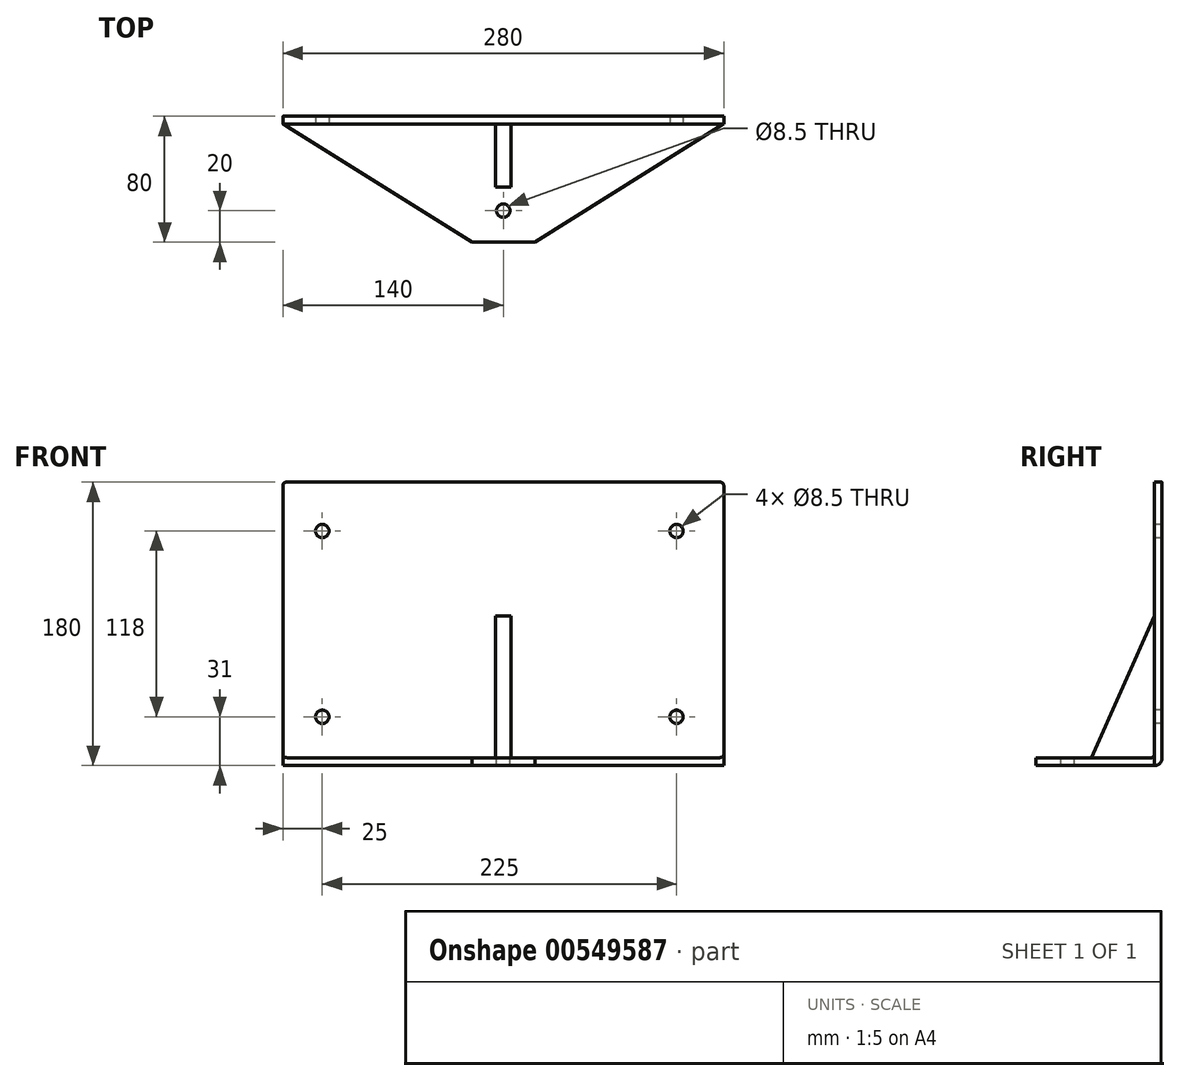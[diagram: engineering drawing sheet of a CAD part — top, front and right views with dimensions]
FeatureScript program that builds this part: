
annotation { "Feature Type Name" : "Feature", "Feature Type Description" : "" }
export const myFeature = defineFeature(function(context is Context, id is Id, definition is map)
    precondition{}
    {
        {
            var Q0;
            Q0=qCreatedBy(makeId("Right.planeOp"),FACE);
            var sketch = newSketch(context, id + "F0", { "sketchPlane" : qUnion([Q0])});
            skLineSegment(sketch, "E0", {"start": v(0, 90) * mm, "end": v(0, -90) * mm});
            skLineSegment(sketch, "E1", {"start": v(0, -90) * mm, "end": v(-80, -90) * mm});
            skLineSegment(sketch, "E2", {"start": v(-80, -90) * mm, "end": v(-80, -85) * mm});
            skLineSegment(sketch, "E3", {"start": v(-80, -85) * mm, "end": v(-5, -85) * mm});
            skLineSegment(sketch, "E4", {"start": v(-5, -85) * mm, "end": v(-5, 90) * mm});
            skLineSegment(sketch, "E5", {"start": v(-5, 90) * mm, "end": v(0, 90) * mm});
            skSolve(sketch);
        }
        {
            var Q0;
            Q0=makeQuery(id+"F0.imprint","IMPRINT",FACE,{"disambiguationData":[TD([[makeQuery(id+"F0.imprint","IMPRINT",EDGE,{"derivedFrom":sQuery(id+"F0.wireOp",EDGE,"E0")}),-1.0]])]});
            extrude(context, id + "F1", {"entities" : qUnion([Q0]), "depth" : 280 * mm, "offsetDistance" : 25 * mm});
        }
        {
            var Q0;
            Q0=makeQuery(id+"F1.opExtrude","SWEPT_FACE",FACE,{"disambiguationData":[OSD([sQuery(id+"F0.wireOp",EDGE,"E4")])]});
            var sketch = newSketch(context, id + "F2", { "sketchPlane" : qUnion([Q0])});
            skLineSegment(sketch, "E6", {"start": v(-180.39, 59) * mm, "end": v(443.82, 59) * mm, "construction": true});
            skLineSegment(sketch, "E7", {"start": v(-176.6, -59) * mm, "end": v(457.98, -59) * mm, "construction": true});
            skLineSegment(sketch, "E8", {"start": v(25, 195.64) * mm, "end": v(25, -196.32) * mm, "construction": true});
            skLineSegment(sketch, "E9", {"start": v(250, 193) * mm, "end": v(250, -198.95) * mm, "construction": true});
            skCircle(sketch, "E10", {"center": v(25, 59) * mm, "radius": 4.25 * mm});
            skCircle(sketch, "E11", {"center": v(250, 59) * mm, "radius": 4.25 * mm});
            skCircle(sketch, "E12", {"center": v(250, -59) * mm, "radius": 4.25 * mm});
            skCircle(sketch, "E13", {"center": v(25, -59) * mm, "radius": 4.25 * mm});
            skSolve(sketch);
        }
        {
            var Q0;
            Q0=makeQuery(id+"F2.imprint","IMPRINT",FACE,{"disambiguationData":[TD([[makeQuery(id+"F2.imprint","IMPRINT",EDGE,{"derivedFrom":sQuery(id+"F2.wireOp",EDGE,"E10")}),1.0]])]});
            var Q1;
            Q1=makeQuery(id+"F2.imprint","IMPRINT",FACE,{"disambiguationData":[TD([[makeQuery(id+"F2.imprint","IMPRINT",EDGE,{"derivedFrom":sQuery(id+"F2.wireOp",EDGE,"E13")}),1.0]])]});
            var Q2;
            Q2=makeQuery(id+"F2.imprint","IMPRINT",FACE,{"disambiguationData":[TD([[makeQuery(id+"F2.imprint","IMPRINT",EDGE,{"derivedFrom":sQuery(id+"F2.wireOp",EDGE,"E12")}),1.0]])]});
            var Q3;
            Q3=makeQuery(id+"F2.imprint","IMPRINT",FACE,{"disambiguationData":[TD([[makeQuery(id+"F2.imprint","IMPRINT",EDGE,{"derivedFrom":sQuery(id+"F2.wireOp",EDGE,"E11")}),1.0]])]});
            extrude(context, id + "F3", {"entities" : qUnion([Q0, Q1, Q2, Q3]), "operationType" : NewBodyOperationType.REMOVE, "endBound" : BoundingType.THROUGH_ALL, "oppositeDirection" : true, "depth" : 25 * mm, "offsetDistance" : 25 * mm});
        }
        {
            var Q0;
            Q0=makeQuery(id+"F1.opExtrude","CAP_EDGE",EDGE,{"disambiguationData":[OSD([sQuery(id+"F0.wireOp",EDGE,"E5")])],"isStart":true});
            var Q1;
            Q1=makeQuery(id+"F1.opExtrude","CAP_EDGE",EDGE,{"disambiguationData":[OSD([sQuery(id+"F0.wireOp",EDGE,"E5")])],"isStart":false});
            var Q2;
            Q2=makeQuery(id+"F1.opExtrude","CAP_EDGE",EDGE,{"disambiguationData":[OSD([sQuery(id+"F0.wireOp",EDGE,"E2")])],"isStart":false});
            var Q3;
            Q3=makeQuery(id+"F1.opExtrude","CAP_EDGE",EDGE,{"disambiguationData":[OSD([sQuery(id+"F0.wireOp",EDGE,"E2")])],"isStart":true});
            fillet(context, id + "F4", {"entities" : qUnion([Q0, Q1, Q2, Q3]), "radius" : 2 * mm, "tangentPropagation" : true, "allowEdgeOverflow" : false});
        }
        {
            var Q0;
            Q0=makeQuery(id+"F1.opExtrude","SWEPT_FACE",FACE,{"disambiguationData":[OSD([sQuery(id+"F0.wireOp",EDGE,"E3")])]});
            var sketch = newSketch(context, id + "F5", { "sketchPlane" : qUnion([Q0])});
            skLineSegment(sketch, "E14", {"start": v(40.82, -60) * mm, "end": v(230.6, -60) * mm, "construction": true});
            skLineSegment(sketch, "E15", {"start": v(140, -5) * mm, "end": v(140, -80) * mm, "construction": true});
            skCircle(sketch, "E16", {"center": v(140, -60) * mm, "radius": 4.25 * mm});
            skSolve(sketch);
        }
        {
            var Q0;
            Q0=makeQuery(id+"F5.imprint","IMPRINT",FACE,{"disambiguationData":[TD([[makeQuery(id+"F5.imprint","IMPRINT",EDGE,{"derivedFrom":sQuery(id+"F5.wireOp",EDGE,"E16")}),1.0]])]});
            extrude(context, id + "F6", {"entities" : qUnion([Q0]), "operationType" : NewBodyOperationType.REMOVE, "endBound" : BoundingType.THROUGH_ALL, "oppositeDirection" : true, "depth" : 25 * mm, "offsetDistance" : 25 * mm});
        }
        {
            var Q0;
            Q0=makeQuery(id+"F1.opExtrude","SWEPT_EDGE",EDGE,{"disambiguationData":[OSD([sQuery(id+"F0.wireOp",EDGE,"E0"),sQuery(id+"F0.wireOp",EDGE,"E1")])]});
            fillet(context, id + "F7", {"entities" : qUnion([Q0]), "radius" : 5 * mm, "tangentPropagation" : true, "allowEdgeOverflow" : false});
        }
        {
            var Q0;
            Q0=makeQuery(id+"F1.opExtrude","SWEPT_FACE",FACE,{"disambiguationData":[OSD([sQuery(id+"F0.wireOp",EDGE,"E4")])]});
            var sketch = newSketch(context, id + "F8", { "sketchPlane" : qUnion([Q0])});
            skLineSegment(sketch, "E17.bottom", {"start": v(135, -85) * mm, "end": v(145, -85) * mm});
            skLineSegment(sketch, "E17.top", {"start": v(135, 5) * mm, "end": v(145, 5) * mm});
            skLineSegment(sketch, "E17.left", {"start": v(135, -85) * mm, "end": v(135, 5) * mm});
            skLineSegment(sketch, "E17.right", {"start": v(145, -85) * mm, "end": v(145, 5) * mm});
            skSolve(sketch);
        }
        {
            var Q0;
            Q0=makeQuery(id+"F8.imprint","IMPRINT",FACE,{"disambiguationData":[TD([[makeQuery(id+"F8.imprint","IMPRINT",EDGE,{"derivedFrom":sQuery(id+"F8.wireOp",EDGE,"E17.bottom")}),-1.0]])]});
            extrude(context, id + "F9", {"entities" : qUnion([Q0]), "operationType" : NewBodyOperationType.ADD, "depth" : 40 * mm, "offsetDistance" : 25 * mm});
        }
        {
            var Q0;
            Q0=makeQuery(id+"F9.opExtrude","SWEPT_FACE",FACE,{"disambiguationData":[OSD([sQuery(id+"F8.wireOp",EDGE,"E17.right")])]});
            var sketch = newSketch(context, id + "F10", { "sketchPlane" : qUnion([Q0])});
            skLineSegment(sketch, "E18", {"start": v(-5, 5) * mm, "end": v(-45, -85) * mm});
            skSolve(sketch);
        }
        {
            var Q0;
            Q0=makeQuery(id+"F10.imprint","IMPRINT",FACE,{"disambiguationData":[TD([[makeQuery(id+"F10.imprint","IMPRINT",EDGE,{"derivedFrom":sQuery(id+"F10.wireOp",EDGE,"E18")}),-1.0]])]});
            extrude(context, id + "F11", {"entities" : qUnion([Q0]), "operationType" : NewBodyOperationType.REMOVE, "endBound" : BoundingType.THROUGH_ALL, "oppositeDirection" : true, "depth" : 25 * mm, "offsetDistance" : 25 * mm});
        }
        {
            var Q0;
            Q0=makeQuery(id+"F1.opExtrude","SWEPT_FACE",FACE,{"disambiguationData":[OSD([sQuery(id+"F0.wireOp",EDGE,"E3")])]});
            var sketch = newSketch(context, id + "F12", { "sketchPlane" : qUnion([Q0])});
            skLineSegment(sketch, "E19.bottom", {"start": v(160, -80) * mm, "end": v(120, -80) * mm, "construction": true});
            skLineSegment(sketch, "E19.top", {"start": v(160, -40) * mm, "end": v(120, -40) * mm, "construction": true});
            skLineSegment(sketch, "E19.left", {"start": v(160, -80) * mm, "end": v(160, -40) * mm, "construction": true});
            skLineSegment(sketch, "E19.right", {"start": v(120, -80) * mm, "end": v(120, -40) * mm, "construction": true});
            skPoint(sketch, "E19.middle", {"position": v(140, -60) * mm});
            skLineSegment(sketch, "E20", {"start": v(280, -5) * mm, "end": v(160, -80) * mm});
            skLineSegment(sketch, "E21", {"start": v(0, -5) * mm, "end": v(120, -80) * mm});
            skSolve(sketch);
        }
        {
            var Q0;
            {var subQ0=sQuery(id+"F12.wireOp",EDGE,"E21");Q0=makeQuery(id+"F12.imprint","IMPRINT",FACE,{"disambiguationData":[TD([[makeQuery(id+"F12.imprint","IMPRINT",EDGE,{"derivedFrom":subQ0}),-1.0]])]});}
            var Q1;
            {var subQ0=sQuery(id+"F12.wireOp",EDGE,"E20");Q1=makeQuery(id+"F12.imprint","IMPRINT",FACE,{"disambiguationData":[TD([[makeQuery(id+"F12.imprint","IMPRINT",EDGE,{"derivedFrom":subQ0}),1.0]])]});}
            extrude(context, id + "F13", {"entities" : qUnion([Q0, Q1]), "operationType" : NewBodyOperationType.REMOVE, "endBound" : BoundingType.THROUGH_ALL, "oppositeDirection" : true, "depth" : 25 * mm, "offsetDistance" : 25 * mm});
        }
        {
            var Q0;
            {var subQ0=sQuery(id+"F0.wireOp",EDGE,"E4");var subQ1=sQuery(id+"F0.wireOp",EDGE,"E3");Q0=makeQuery(id+"F9.boolean.opBoolean","SPLIT",EDGE,{"disambiguationData":[TD([makeQuery(id+"F9.opExtrude","SWEPT_FACE",FACE,{"disambiguationData":[OSD([sQuery(id+"F8.wireOp",EDGE,"E17.left")])]})])],"derivedFrom":makeQuery(id+"F1.opExtrude","SWEPT_EDGE",EDGE,{"disambiguationData":[OSD([subQ1,subQ0])]})});}
            var Q1;
            {var subQ0=sQuery(id+"F0.wireOp",EDGE,"E4");var subQ1=sQuery(id+"F0.wireOp",EDGE,"E3");Q1=makeQuery(id+"F9.boolean.opBoolean","SPLIT",EDGE,{"disambiguationData":[TD([makeQuery(id+"F9.opExtrude","SWEPT_FACE",FACE,{"disambiguationData":[OSD([sQuery(id+"F8.wireOp",EDGE,"E17.right")])]})])],"derivedFrom":makeQuery(id+"F1.opExtrude","SWEPT_EDGE",EDGE,{"disambiguationData":[OSD([subQ1,subQ0])]})});}
            fillet(context, id + "F14", {"entities" : qUnion([Q0, Q1]), "radius" : 2 * mm, "tangentPropagation" : true, "allowEdgeOverflow" : false});
        }
    });
